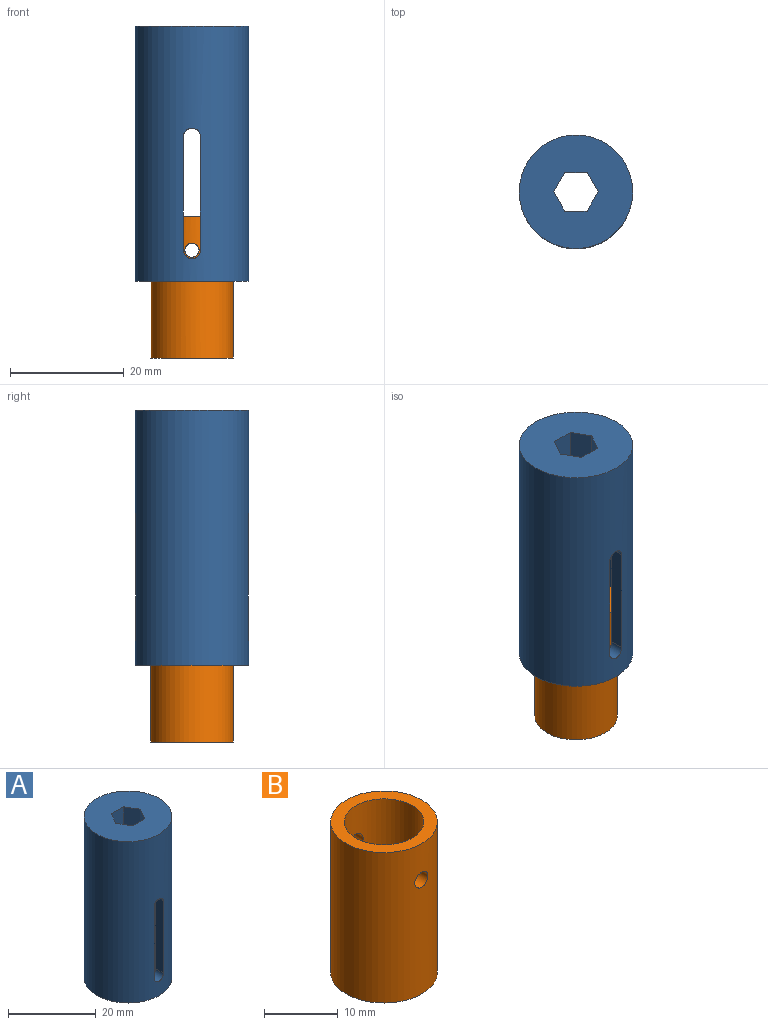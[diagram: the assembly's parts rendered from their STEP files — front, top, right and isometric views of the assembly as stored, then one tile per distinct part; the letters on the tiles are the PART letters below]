
ASSEMBLY  parts=2 mates=1
PART A: 19 faces, bbox 20x20x45 mm
  f0: plane 5x3.39mm, normal (-0.86,0.5,0), area 19.6mm2, adj f1,f5,f8,f10
  f1: plane 5x3.41mm, normal (-0.87,-0.5,0), area 19.6mm2, adj f0,f2,f8,f10
  f2: plane 5x3.93mm, normal (0,-1,0), area 19.6mm2, adj f1,f3,f8,f10
  f3: plane 5x3.39mm, normal (0.86,-0.5,0), area 19.6mm2, adj f2,f4,f8,f10
  f4: plane 5x3.41mm, normal (0.87,0.5,0), area 19.6mm2, adj f3,f5,f8,f10
  f5: plane 5x3.93mm, normal (0,1,0), area 19.6mm2, adj f0,f4,f8,f10
  f6: cylinder r=10mm len=45mm, axis (0,0,1), area 2692.8mm2, adj f7,f8,f11,f12,f13,f14,f15,f16
  f7: plane 20x20mm, normal (0,0,-1), area 137.4mm2, adj f6,f9
  f8: plane 20x20mm, normal (0,0,1), area 274.1mm2, adj f0,f1,f2,f3,f4,f5,f6
  f9: cylinder r=7.5mm len=40mm, axis (0,0,-1), area 1749.9mm2, adj f7,f10,f11,f12,f13,f14,f15,f16
  f10: plane 15x15mm, normal (0,0,-1), area 136.7mm2, adj f0,f1,f2,f3,f4,f5,f9
  f11: cylinder r=1.5mm len=3mm, axis (0,-1,0), area 11.9mm2, adj f6,f9,f12,f14
  f12: plane 20x2.54mm, normal (-1,0,0), area 50.8mm2, adj f6,f9,f11,f13
  f13: cylinder r=1.5mm len=3mm, axis (0,-1,0), area 11.9mm2, adj f6,f9,f12,f14
  f14: plane 20x2.54mm, normal (1,0,0), area 50.8mm2, adj f6,f9,f11,f13
  f15: plane 20x2.54mm, normal (1,0,0), area 50.8mm2, adj f6,f9,f16,f18
  f16: cylinder r=1.5mm len=3mm, axis (0,-1,0), area 11.9mm2, adj f6,f9,f15,f17
  f17: plane 20x2.54mm, normal (-1,0,0), area 50.8mm2, adj f6,f9,f16,f18
  f18: cylinder r=1.5mm len=3mm, axis (0,-1,0), area 11.9mm2, adj f6,f9,f15,f17
PART B: 6 faces, bbox 14.5x14.5x25 mm
  f0: cylinder r=5.4mm len=25mm, axis (0,0,-1), area 838.3mm2, adj f2,f3,f4,f5
  f1: cylinder r=7.25mm len=25mm, axis (0,0,-1), area 1128.9mm2, adj f2,f3,f4,f5
  f2: plane 14.5x14.5mm, normal (0,0,1), area 73.5mm2, adj f0,f1
  f3: plane 14.5x14.5mm, normal (0,0,-1), area 73.5mm2, adj f0,f1
  f4: cylinder r=1.25mm len=2.5mm, axis (0,-1,0), area 14.7mm2, adj f0,f1
  f5: cylinder r=1.25mm len=2.5mm, axis (0,-1,0), area 14.7mm2, adj f0,f1
PLACE A t=(-7.38,-13.23,15.04)mm
PLACE B t=(-7.38,-13.23,-43.46)mm
MATE slider B.f1 <-> A.f9  axis (0,0,-1) through (-7.38,-13.23,-43.46)mm
